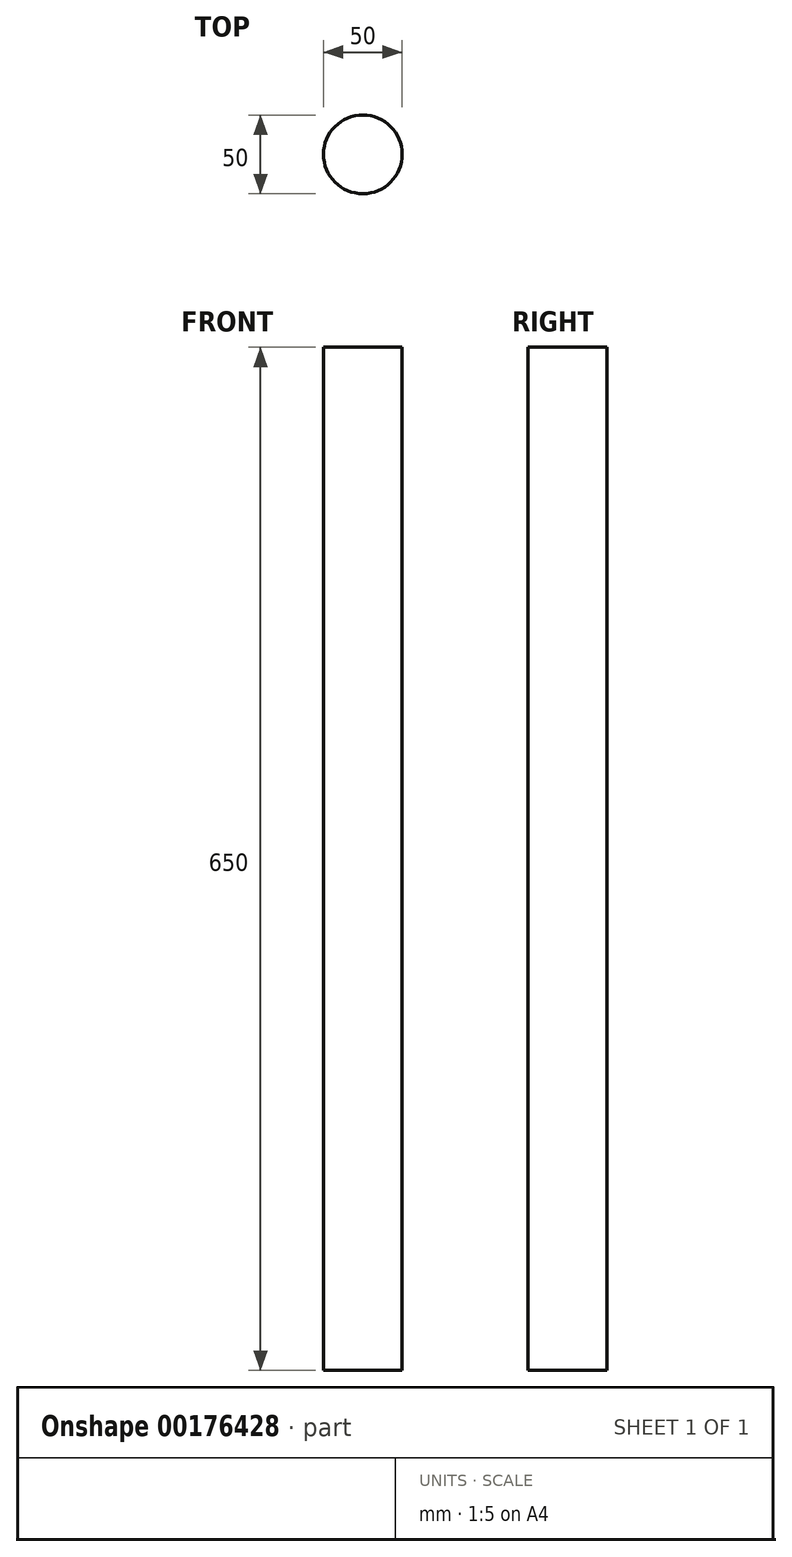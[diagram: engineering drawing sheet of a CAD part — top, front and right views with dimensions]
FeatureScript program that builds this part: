
annotation { "Feature Type Name" : "Feature", "Feature Type Description" : "" }
export const myFeature = defineFeature(function(context is Context, id is Id, definition is map)
    precondition{}
    {
        {
            var Q0;
            Q0=qCreatedBy(makeId("Top.planeOp"),FACE);
            var sketch = newSketch(context, id + "F0", { "sketchPlane" : qUnion([Q0])});
            skCircle(sketch, "E0", {"center": v(0, 0) * mm, "radius": 25 * mm});
            skLineSegment(sketch, "E1", {"start": v(-35.59, -35.5) * mm, "end": v(48.76, -35.5) * mm});
            skSolve(sketch);
        }
        {
            var Q0;
            Q0 = qSketchRegion(id + "F0", true);
            extrude(context, id + "F1", {"entities" : qUnion([Q0]), "oppositeDirection" : true, "depth" : 650 * mm});
        }
    });
